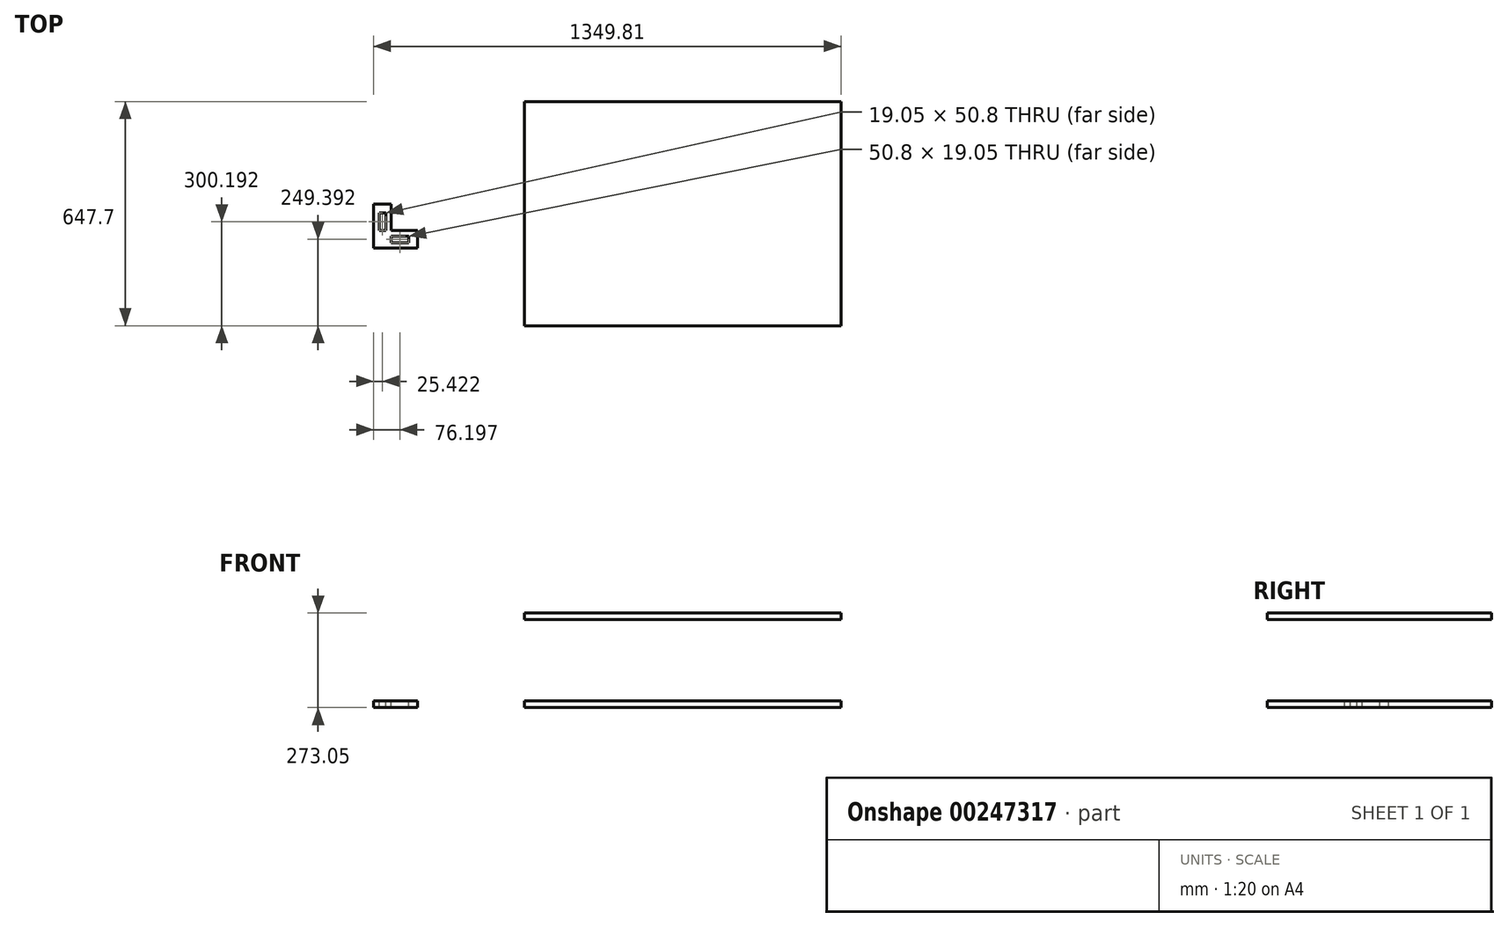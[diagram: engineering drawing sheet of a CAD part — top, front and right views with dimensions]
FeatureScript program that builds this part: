
annotation { "Feature Type Name" : "Feature", "Feature Type Description" : "" }
export const myFeature = defineFeature(function(context is Context, id is Id, definition is map)
    precondition{}
    {
        {
            var Q0;
            Q0=qCreatedBy(makeId("Top.planeOp"),FACE);
            var sketch = newSketch(context, id + "F0", { "sketchPlane" : qUnion([Q0])});
            skLineSegment(sketch, "E0.bottom", {"start": v(0, 0) * mm, "end": v(914.4, 0) * mm});
            skLineSegment(sketch, "E0.top", {"start": v(0, 647.7) * mm, "end": v(914.4, 647.7) * mm});
            skLineSegment(sketch, "E0.left", {"start": v(0, 0) * mm, "end": v(0, 647.7) * mm});
            skLineSegment(sketch, "E0.right", {"start": v(914.4, 0) * mm, "end": v(914.4, 647.7) * mm});
            skSolve(sketch);
        }
        {
            var Q0;
            Q0=makeQuery(id+"F0.imprint","IMPRINT",FACE,{"disambiguationData":[TD([[makeQuery(id+"F0.imprint","IMPRINT",EDGE,{"derivedFrom":sQuery(id+"F0.wireOp",EDGE,"E0.bottom")}),1.0]])]});
            extrude(context, id + "F1", {"entities" : qUnion([Q0]), "oppositeDirection" : true, "depth" : 19.05 * mm});
        }
        {
            var Q0;
            Q0=makeQuery(id+"F1.opExtrude","SWEPT_BODY",BODY,{"disambiguationData":[OSD([sQuery(id+"F0.wireOp",EDGE,"E0.bottom"),sQuery(id+"F0.wireOp",EDGE,"E0.top"),sQuery(id+"F0.wireOp",EDGE,"E0.left"),sQuery(id+"F0.wireOp",EDGE,"E0.right")])]});
            transform(context, id + "F2", {"entities" : qUnion([Q0]), "transformType" : TransformType.TRANSLATION_3D, "dx" : 0 * mm, "dy" : 0 * mm, "dz" : 254 * mm, "makeCopy" : true});
        }
        {
            var Q0;
            Q0=makeQuery(id+"F1.opExtrude","CAP_FACE",FACE,{"disambiguationData":[OSD([sQuery(id+"F0.wireOp",EDGE,"E0.bottom"),sQuery(id+"F0.wireOp",EDGE,"E0.top"),sQuery(id+"F0.wireOp",EDGE,"E0.left"),sQuery(id+"F0.wireOp",EDGE,"E0.right")])],"isStart":true});
            var sketch = newSketch(context, id + "F3", { "sketchPlane" : qUnion([Q0])});
            skLineSegment(sketch, "E1", {"start": v(-435.41, 351) * mm, "end": v(-435.41, 224) * mm});
            skLineSegment(sketch, "E2", {"start": v(-435.41, 224) * mm, "end": v(-308.41, 224) * mm});
            skLineSegment(sketch, "E3", {"start": v(-308.41, 224) * mm, "end": v(-308.41, 274.8) * mm});
            skLineSegment(sketch, "E4", {"start": v(-308.41, 274.8) * mm, "end": v(-384.61, 274.8) * mm});
            skLineSegment(sketch, "E5", {"start": v(-384.61, 274.8) * mm, "end": v(-384.61, 351) * mm});
            skLineSegment(sketch, "E6", {"start": v(-384.61, 351) * mm, "end": v(-435.41, 351) * mm});
            skLineSegment(sketch, "E7", {"start": v(-419.51, 325.6) * mm, "end": v(-400.46, 325.6) * mm});
            skLineSegment(sketch, "E8", {"start": v(-400.46, 325.6) * mm, "end": v(-400.46, 274.8) * mm});
            skLineSegment(sketch, "E9", {"start": v(-400.46, 274.8) * mm, "end": v(-419.51, 274.8) * mm});
            skLineSegment(sketch, "E10", {"start": v(-419.51, 274.8) * mm, "end": v(-419.51, 325.6) * mm});
            skLineSegment(sketch, "E11.bottom", {"start": v(-384.61, 258.92) * mm, "end": v(-333.81, 258.92) * mm});
            skLineSegment(sketch, "E11.top", {"start": v(-384.61, 239.87) * mm, "end": v(-333.81, 239.87) * mm});
            skLineSegment(sketch, "E11.left", {"start": v(-384.61, 258.92) * mm, "end": v(-384.61, 239.87) * mm});
            skLineSegment(sketch, "E11.right", {"start": v(-333.81, 258.92) * mm, "end": v(-333.81, 239.87) * mm});
            skSolve(sketch);
        }
        {
            var Q0;
            Q0=makeQuery(id+"F3.imprint","IMPRINT",FACE,{"disambiguationData":[TD([[makeQuery(id+"F3.imprint","IMPRINT",EDGE,{"derivedFrom":sQuery(id+"F3.wireOp",EDGE,"E1")}),1.0]])]});
            extrude(context, id + "F4", {"entities" : qUnion([Q0]), "oppositeDirection" : true, "depth" : 19.05 * mm});
        }
    });
